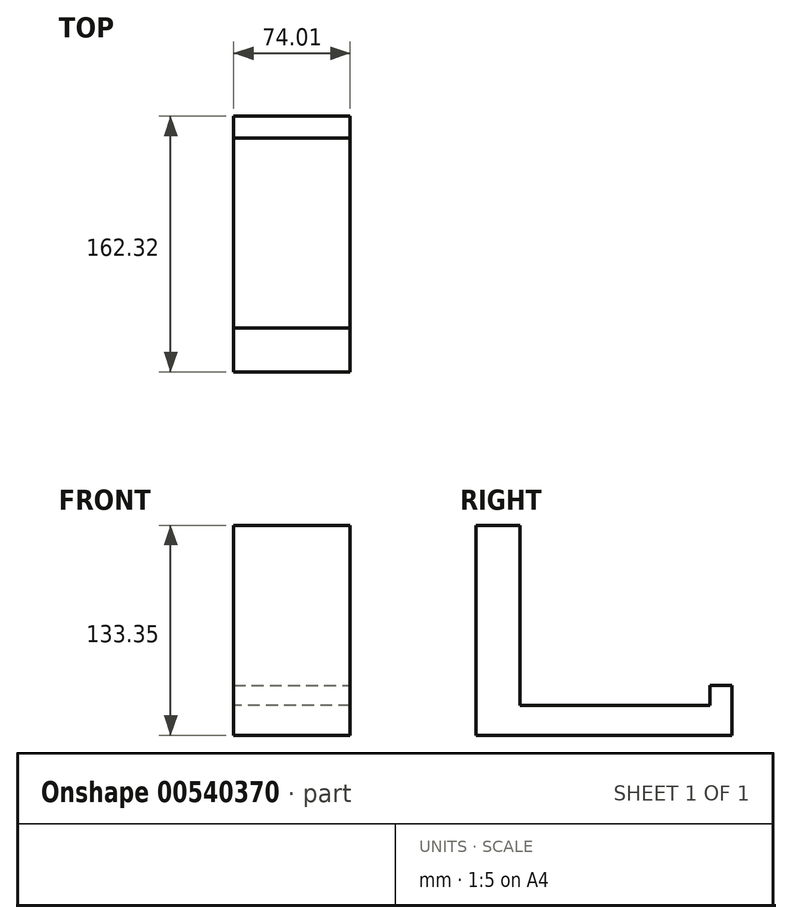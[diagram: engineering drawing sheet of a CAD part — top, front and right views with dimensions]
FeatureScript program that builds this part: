
annotation { "Feature Type Name" : "Feature", "Feature Type Description" : "" }
export const myFeature = defineFeature(function(context is Context, id is Id, definition is map)
    precondition{}
    {
        {
            var Q0;
            Q0=qCreatedBy(makeId("Top.planeOp"),FACE);
            var sketch = newSketch(context, id + "F0", { "sketchPlane" : qUnion([Q0])});
            skLineSegment(sketch, "E0.bottom", {"start": v(-42.5, 36.68) * mm, "end": v(31.5, 36.68) * mm});
            skLineSegment(sketch, "E0.top", {"start": v(-42.5, -74.84) * mm, "end": v(31.5, -74.84) * mm});
            skLineSegment(sketch, "E0.left", {"start": v(-42.5, 36.68) * mm, "end": v(-42.5, -74.84) * mm});
            skLineSegment(sketch, "E0.right", {"start": v(31.5, 36.68) * mm, "end": v(31.5, -74.84) * mm});
            skSolve(sketch);
        }
        {
            var Q0;
            Q0 = qSketchRegion(id + "F0", true);
            extrude(context, id + "F1", {"entities" : qUnion([Q0]), "depth" : 19.05 * mm, "offsetDistance" : 25.4 * mm});
        }
        {
            var Q0;
            Q0=makeQuery(id+"F1.opExtrude","CAP_FACE",FACE,{"disambiguationData":[OSD([sQuery(id+"F0.wireOp",EDGE,"E0.bottom"),sQuery(id+"F0.wireOp",EDGE,"E0.top"),sQuery(id+"F0.wireOp",EDGE,"E0.left"),sQuery(id+"F0.wireOp",EDGE,"E0.right")])],"isStart":false});
            var sketch = newSketch(context, id + "F2", { "sketchPlane" : qUnion([Q0])});
            skLineSegment(sketch, "E1.bottom", {"start": v(31.5, -74.84) * mm, "end": v(-42.5, -74.84) * mm});
            skLineSegment(sketch, "E1.top", {"start": v(31.5, -47) * mm, "end": v(-42.5, -47) * mm});
            skLineSegment(sketch, "E1.left", {"start": v(31.5, -74.84) * mm, "end": v(31.5, -47) * mm});
            skLineSegment(sketch, "E1.right", {"start": v(-42.5, -74.84) * mm, "end": v(-42.5, -47) * mm});
            skSolve(sketch);
        }
        {
            var Q0;
            Q0 = qSketchRegion(id + "F2", true);
            extrude(context, id + "F3", {"entities" : qUnion([Q0]), "operationType" : NewBodyOperationType.ADD, "depth" : 114.3 * mm, "offsetDistance" : 25.4 * mm});
        }
        {
            var Q0;
            Q0=makeQuery(id+"F1.opExtrude","SWEPT_FACE",FACE,{"disambiguationData":[OSD([sQuery(id+"F0.wireOp",EDGE,"E0.bottom")])]});
            extrude(context, id + "F4", {"entities" : qUnion([Q0]), "operationType" : NewBodyOperationType.ADD, "depth" : 50.8 * mm, "offsetDistance" : 25.4 * mm});
        }
        {
            var Q0;
            {var subQ0=sQuery(id+"F0.wireOp",EDGE,"E0.bottom");Q0=makeQuery(id+"F4.boolean.opBoolean","MERGE",FACE,{"derivedFrom":[makeQuery(id+"F1.opExtrude","CAP_FACE",FACE,{"disambiguationData":[OSD([subQ0,sQuery(id+"F0.wireOp",EDGE,"E0.top"),sQuery(id+"F0.wireOp",EDGE,"E0.left"),sQuery(id+"F0.wireOp",EDGE,"E0.right")])],"isStart":false}),makeQuery(id+"F4.opExtrude","SWEPT_FACE",FACE,{"disambiguationData":[OSD([subQ0]),TDD([makeQuery(id+"F1.opExtrude","CAP_EDGE",EDGE,{"disambiguationData":[OSD([subQ0])],"isStart":false})])]})]});}
            var sketch = newSketch(context, id + "F5", { "sketchPlane" : qUnion([Q0])});
            skLineSegment(sketch, "E2.bottom", {"start": v(31.5, 73.61) * mm, "end": v(-42.5, 73.61) * mm});
            skLineSegment(sketch, "E2.top", {"start": v(31.5, 87.48) * mm, "end": v(-42.5, 87.48) * mm});
            skLineSegment(sketch, "E2.left", {"start": v(31.5, 73.61) * mm, "end": v(31.5, 87.48) * mm});
            skLineSegment(sketch, "E2.right", {"start": v(-42.5, 73.61) * mm, "end": v(-42.5, 87.48) * mm});
            skSolve(sketch);
        }
        {
            var Q0;
            Q0 = qSketchRegion(id + "F5", true);
            extrude(context, id + "F6", {"entities" : qUnion([Q0]), "operationType" : NewBodyOperationType.ADD, "depth" : 12.7 * mm, "offsetDistance" : 25.4 * mm});
        }
    });
